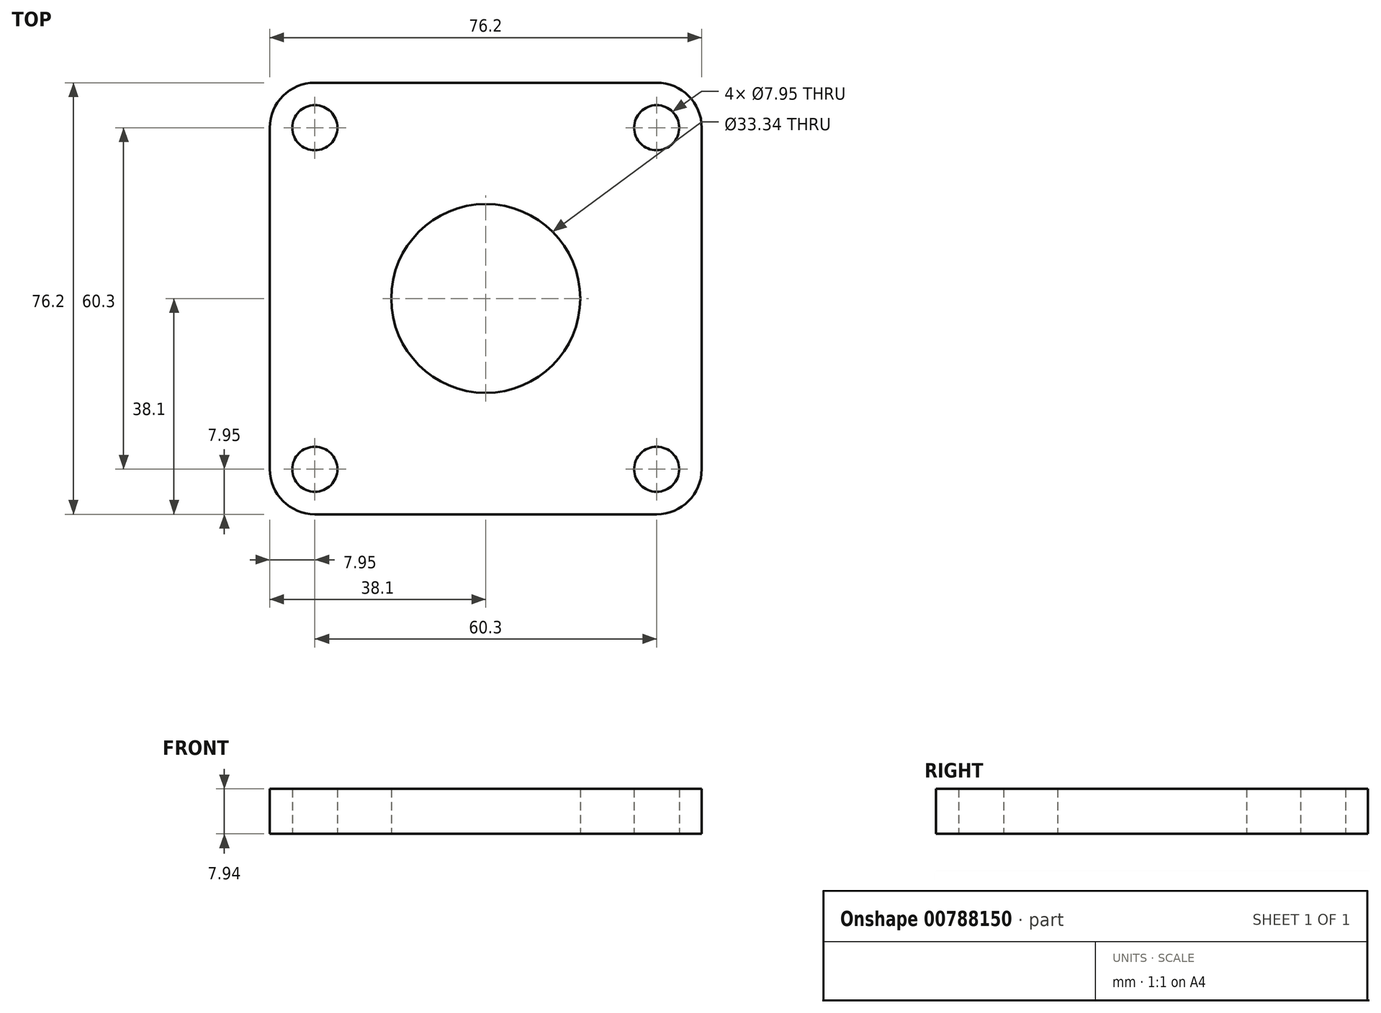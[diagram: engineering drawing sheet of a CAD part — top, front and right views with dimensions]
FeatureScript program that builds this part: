
annotation { "Feature Type Name" : "Feature", "Feature Type Description" : "" }
export const myFeature = defineFeature(function(context is Context, id is Id, definition is map)
    precondition{}
    {
        {
            var Q0;
            Q0=qCreatedBy(makeId("Top.planeOp"),FACE);
            var sketch = newSketch(context, id + "F0", { "sketchPlane" : qUnion([Q0])});
            skLineSegment(sketch, "E0.bottom", {"start": v(30.15, -38.1) * mm, "end": v(-30.15, -38.1) * mm});
            skLineSegment(sketch, "E0.top", {"start": v(30.15, 38.1) * mm, "end": v(-30.15, 38.1) * mm});
            skLineSegment(sketch, "E0.left", {"start": v(38.1, -30.15) * mm, "end": v(38.1, 30.15) * mm});
            skLineSegment(sketch, "E0.right", {"start": v(-38.1, -30.15) * mm, "end": v(-38.1, 30.15) * mm});
            skPoint(sketch, "E0.middle", {"position": v(0, 0) * mm});
            skCircle(sketch, "E1", {"center": v(0, 0) * mm, "radius": 16.67 * mm});
            skPoint(sketch, "E2.visualSharp", {"position": v(-38.1, 38.1) * mm});
            skArc(sketch, "E2.filletArc", {"start": v(-30.15, 38.1) * mm, "mid": v(-35.77, 35.77) * mm, "end": v(-38.1, 30.15) * mm});
            skPoint(sketch, "E3.visualSharp", {"position": v(38.1, 38.1) * mm});
            skArc(sketch, "E3.filletArc", {"start": v(38.1, 30.15) * mm, "mid": v(35.77, 35.77) * mm, "end": v(30.15, 38.1) * mm});
            skPoint(sketch, "E4.visualSharp", {"position": v(38.1, -38.1) * mm});
            skArc(sketch, "E4.filletArc", {"start": v(30.15, -38.1) * mm, "mid": v(35.77, -35.77) * mm, "end": v(38.1, -30.15) * mm});
            skPoint(sketch, "E5.visualSharp", {"position": v(-38.1, -38.1) * mm});
            skArc(sketch, "E5.filletArc", {"start": v(-38.1, -30.15) * mm, "mid": v(-35.77, -35.77) * mm, "end": v(-30.15, -38.1) * mm});
            skCircle(sketch, "E6", {"center": v(-30.15, -30.15) * mm, "radius": 3.98 * mm});
            skCircle(sketch, "E7", {"center": v(30.15, -30.15) * mm, "radius": 3.98 * mm});
            skCircle(sketch, "E8", {"center": v(-30.15, 30.15) * mm, "radius": 3.98 * mm});
            skCircle(sketch, "E9", {"center": v(30.15, 30.15) * mm, "radius": 3.98 * mm});
            skSolve(sketch);
        }
        {
            var Q0;
            Q0=makeQuery(id+"F0.imprint","IMPRINT",FACE,{"disambiguationData":[TD([[makeQuery(id+"F0.imprint","IMPRINT",EDGE,{"derivedFrom":sQuery(id+"F0.wireOp",EDGE,"E0.bottom")}),-1.0]])]});
            extrude(context, id + "F1", {"entities" : qUnion([Q0]), "depth" : 7.94 * mm, "offsetDistance" : 25.4 * mm});
        }
    });
